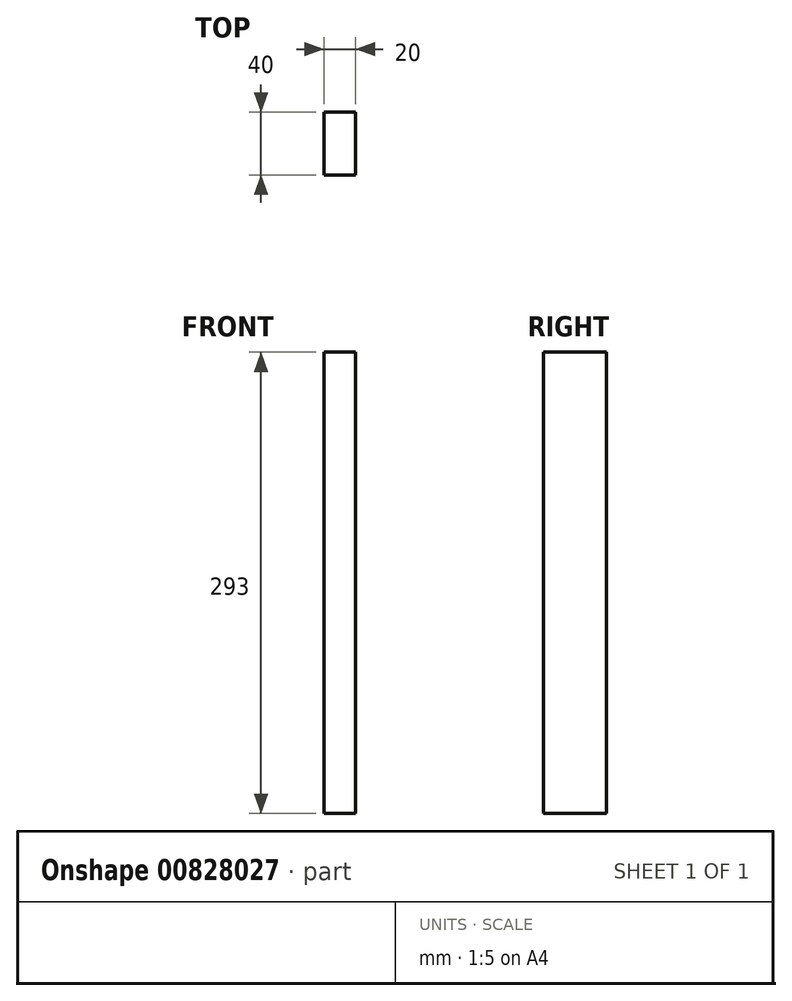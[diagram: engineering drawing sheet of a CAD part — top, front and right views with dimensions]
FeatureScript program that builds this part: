
annotation { "Feature Type Name" : "Feature", "Feature Type Description" : "" }
export const myFeature = defineFeature(function(context is Context, id is Id, definition is map)
    precondition{}
    {
        {
            var Q0;
            Q0=qCreatedBy(makeId("Front.planeOp"),FACE);
            var sketch = newSketch(context, id + "F0", { "sketchPlane" : qUnion([Q0])});
            skLineSegment(sketch, "E0.bottom", {"start": v(0, 0) * mm, "end": v(20, 0) * mm});
            skLineSegment(sketch, "E0.top", {"start": v(0, 293) * mm, "end": v(20, 293) * mm});
            skLineSegment(sketch, "E0.left", {"start": v(0, 0) * mm, "end": v(0, 293) * mm});
            skLineSegment(sketch, "E0.right", {"start": v(20, 0) * mm, "end": v(20, 293) * mm});
            skSolve(sketch);
        }
        {
            var Q0;
            Q0=makeQuery(id+"F0.imprint","IMPRINT",FACE,{"disambiguationData":[TD([[makeQuery(id+"F0.imprint","IMPRINT",EDGE,{"derivedFrom":sQuery(id+"F0.wireOp",EDGE,"E0.bottom")}),1.0]])]});
            extrude(context, id + "F1", {"entities" : qUnion([Q0]), "depth" : 40 * mm, "offsetDistance" : 25 * mm});
        }
    });
